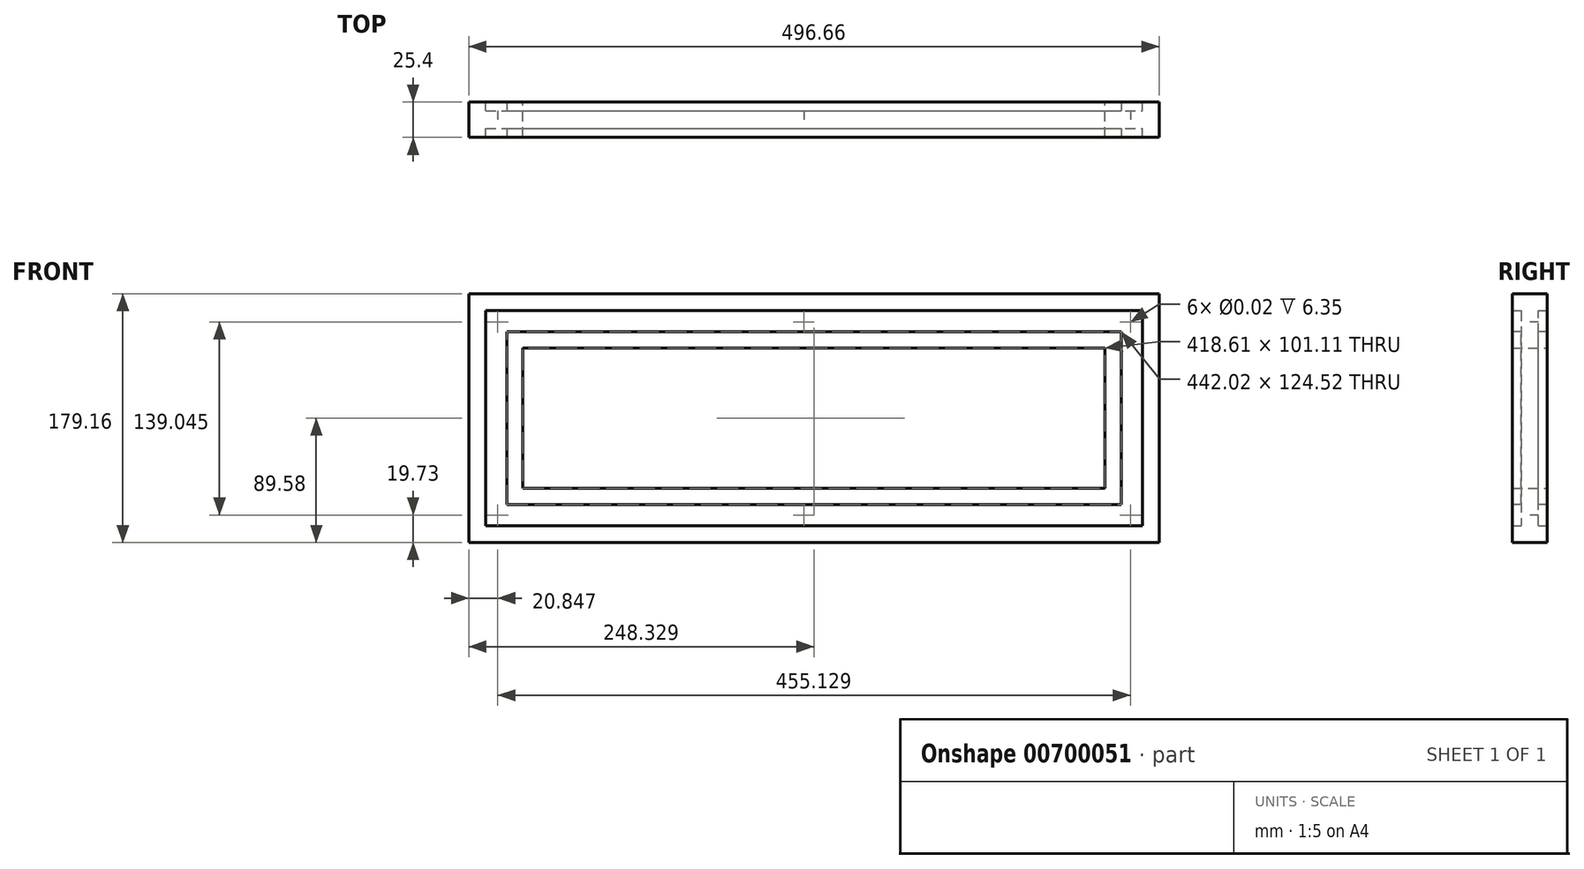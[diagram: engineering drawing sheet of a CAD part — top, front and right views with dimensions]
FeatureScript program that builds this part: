
annotation { "Feature Type Name" : "Feature", "Feature Type Description" : "" }
export const myFeature = defineFeature(function(context is Context, id is Id, definition is map)
    precondition{}
    {
        {
            var Q0;
            Q0=qCreatedBy(makeId("Right.planeOp"),FACE);
            var sketch = newSketch(context, id + "F0", { "sketchPlane" : qUnion([Q0])});
            skLineSegment(sketch, "E0.left", {"start": v(-6.35, -7.6) * mm, "end": v(-6.35, 7.6) * mm});
            skLineSegment(sketch, "E0.right", {"start": v(6.35, -7.6) * mm, "end": v(6.35, 7.6) * mm});
            skPoint(sketch, "E0.middle", {"position": v(0, 0) * mm});
            skLineSegment(sketch, "E1.bottom", {"start": v(-12.7, 7.6) * mm, "end": v(-6.35, 7.6) * mm});
            skLineSegment(sketch, "E1.top", {"start": v(-12.7, 19.3) * mm, "end": v(12.7, 19.3) * mm});
            skLineSegment(sketch, "E1.left", {"start": v(-12.7, 7.6) * mm, "end": v(-12.7, 19.3) * mm});
            skLineSegment(sketch, "E1.right", {"start": v(12.7, 7.6) * mm, "end": v(12.7, 19.3) * mm});
            skPoint(sketch, "E1.middle", {"position": v(0, 13.44) * mm});
            skLineSegment(sketch, "E2.bottom", {"start": v(-12.7, -19.73) * mm, "end": v(12.7, -19.72) * mm});
            skLineSegment(sketch, "E2.left", {"start": v(-12.7, -19.73) * mm, "end": v(-12.7, -7.65) * mm});
            skLineSegment(sketch, "E2.right", {"start": v(12.7, -19.72) * mm, "end": v(12.7, -7.63) * mm});
            skPoint(sketch, "E2.middle", {"position": v(0, -13.68) * mm});
            skLineSegment(sketch, "E3.trimOffspring", {"start": v(6.35, 7.6) * mm, "end": v(12.7, 7.6) * mm});
            skLineSegment(sketch, "E4", {"start": v(12.7, -7.63) * mm, "end": v(6.35, -7.6) * mm});
            skLineSegment(sketch, "E5", {"start": v(-6.35, -7.6) * mm, "end": v(-12.7, -7.65) * mm});
            skSolve(sketch);
        }
        {
            var Q0;
            Q0=qCreatedBy(makeId("Front.planeOp"),FACE);
            var sketch = newSketch(context, id + "F1", { "sketchPlane" : qUnion([Q0])});
            skLineSegment(sketch, "E6", {"start": v(0, 0) * mm, "end": v(-221.3, 0) * mm});
            skLineSegment(sketch, "E7", {"start": v(-221.3, 0) * mm, "end": v(-221.3, 139.7) * mm});
            skLineSegment(sketch, "E8", {"start": v(-221.3, 139.7) * mm, "end": v(235.9, 139.7) * mm});
            skLineSegment(sketch, "E9", {"start": v(235.9, 139.7) * mm, "end": v(235.9, 0) * mm});
            skLineSegment(sketch, "E10", {"start": v(235.9, 0) * mm, "end": v(0, 0) * mm});
            skSolve(sketch);
        }
        {
            var Q0;
            Q0=makeQuery(id+"F0.imprint","IMPRINT",FACE,{"disambiguationData":[TD([[makeQuery(id+"F0.imprint","IMPRINT",EDGE,{"derivedFrom":sQuery(id+"F0.wireOp",EDGE,"E0.left")}),-1.0]])]});
            var Q1;
            Q1=sQuery(id+"F1.wireOp",EDGE,"E10");
            var Q2;
            Q2=sQuery(id+"F1.wireOp",EDGE,"E9");
            var Q3;
            Q3=sQuery(id+"F1.wireOp",EDGE,"E8");
            var Q4;
            Q4=sQuery(id+"F1.wireOp",EDGE,"E7");
            var Q5;
            Q5=sQuery(id+"F1.wireOp",EDGE,"E6");
            sweep(context, id + "F2", {"profiles" : qUnion([Q0]), "path" : qUnion([Q1, Q2, Q3, Q4, Q5])});
        }
        {
            var Q0;
            Q0=qCreatedBy(makeId("Front.planeOp"),FACE);
            var sketch = newSketch(context, id + "F3", { "sketchPlane" : qUnion([Q0])});
            skPoint(sketch, "E11", {"position": v(234.96, 139.04) * mm});
            skPoint(sketch, "E12", {"position": v(0, 139.04) * mm});
            skPoint(sketch, "E13", {"position": v(0, 0) * mm});
            skPoint(sketch, "E14", {"position": v(234.96, 0) * mm});
            skPoint(sketch, "E15", {"position": v(-220.17, 139.04) * mm});
            skPoint(sketch, "E16", {"position": v(-220.17, 0) * mm});
            skSolve(sketch);
        }
        {
            var Q0;
            Q0=sQuery(id+"F3.wireOp",VERTEX,"E15");
            var Q1;
            Q1=sQuery(id+"F3.wireOp",VERTEX,"E16");
            var Q2;
            Q2=sQuery(id+"F3.wireOp",VERTEX,"E12");
            var Q3;
            Q3=sQuery(id+"F3.wireOp",VERTEX,"E13");
            var Q4;
            Q4=sQuery(id+"F3.wireOp",VERTEX,"E11");
            var Q5;
            Q5=sQuery(id+"F3.wireOp",VERTEX,"E14");
            var Q6;
            Q6=makeQuery(id+"F2.opSweep","SWEPT_BODY",BODY,{"disambiguationData":[OSD([sQuery(id+"F0.wireOp",EDGE,"E0.left"),sQuery(id+"F0.wireOp",EDGE,"E0.right"),sQuery(id+"F0.wireOp",EDGE,"E1.bottom"),sQuery(id+"F0.wireOp",EDGE,"E1.top"),sQuery(id+"F0.wireOp",EDGE,"E1.left"),sQuery(id+"F0.wireOp",EDGE,"E1.right"),sQuery(id+"F0.wireOp",EDGE,"E2.bottom"),sQuery(id+"F0.wireOp",EDGE,"E2.left"),sQuery(id+"F0.wireOp",EDGE,"E2.right"),sQuery(id+"F0.wireOp",EDGE,"E3.trimOffspring"),sQuery(id+"F0.wireOp",EDGE,"E4"),sQuery(id+"F0.wireOp",EDGE,"E5"),sQuery(id+"F1.wireOp",EDGE,"E9")])]});
            hole(context, id + "F4", {"style" : HoleStyle.SIMPLE, "endStyle" : HoleEndStyle.THROUGH, "standardTappedOrClearance" : lookupTablePath({ "standard" : "ANSI", "size" : "7/16 (0.44)", "type" : "Drilled" }), "standardBlindInLast" : lookupTablePath({ "standard" : "ANSI", "size" : "7/16", "type" : "Drilled" }), "holeDiameter" : 7 / 406.4 * mm, "majorDiameter" : 6.35 * mm, "isTappedThrough" : true, "tappedDepth" : 12.7 * mm, "tapClearance" : 3, "locations" : qUnion([Q0, Q1, Q2, Q3, Q4, Q5]), "scope" : qUnion([Q6])});
        }
    });
